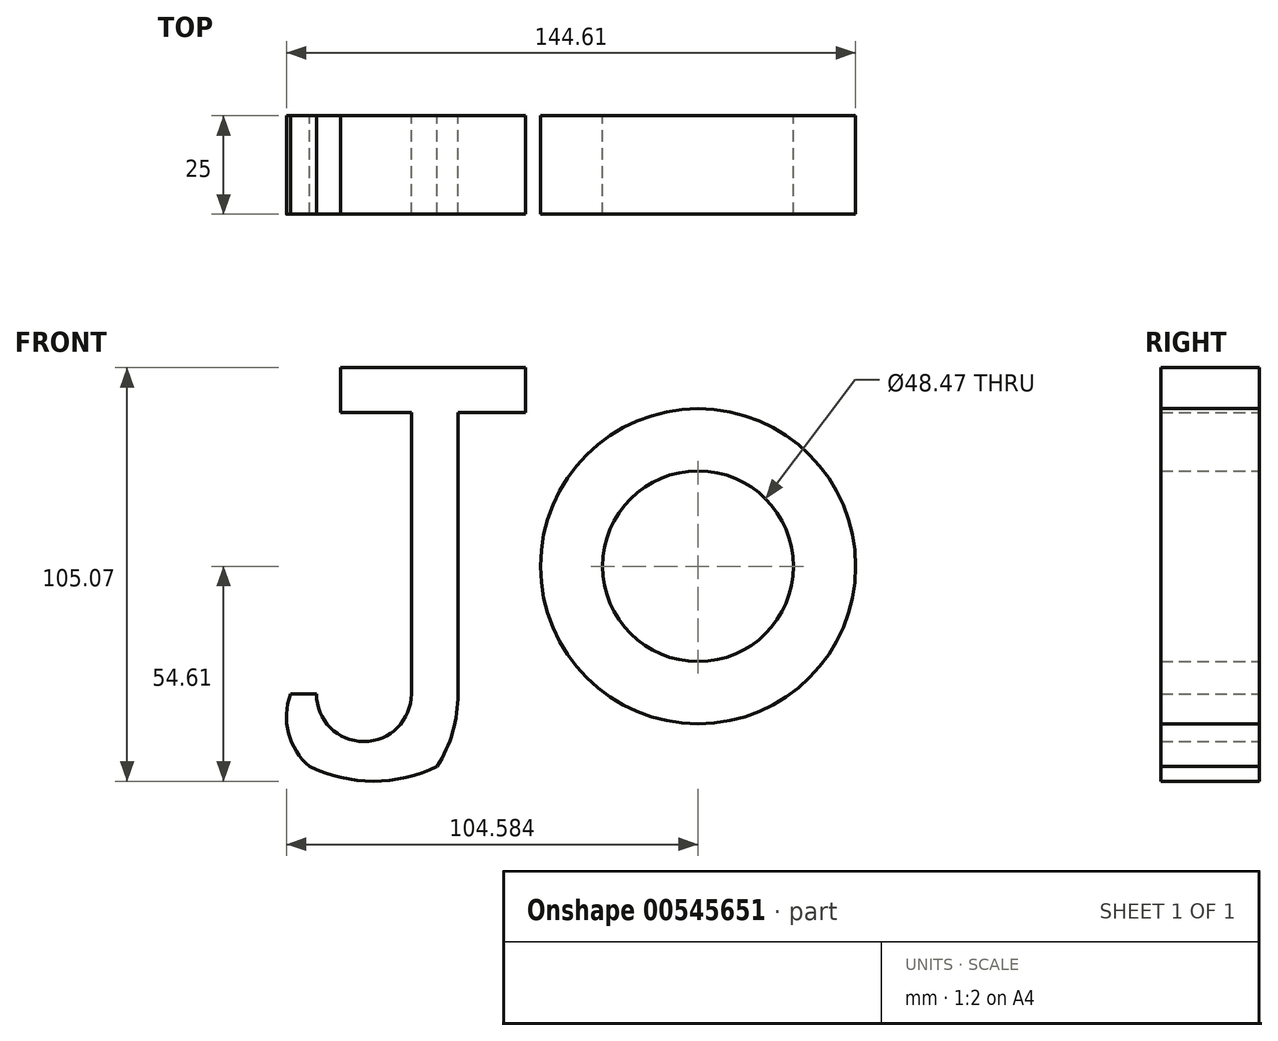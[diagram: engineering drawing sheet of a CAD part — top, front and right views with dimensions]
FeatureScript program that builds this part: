
annotation { "Feature Type Name" : "Feature", "Feature Type Description" : "" }
export const myFeature = defineFeature(function(context is Context, id is Id, definition is map)
    precondition{}
    {
        {
            var Q0;
            Q0=qCreatedBy(makeId("Front.planeOp"),FACE);
            var sketch = newSketch(context, id + "F0", { "sketchPlane" : qUnion([Q0])});
            skLineSegment(sketch, "E0.bottom", {"start": v(-63.19, 50.46) * mm, "end": v(-16.24, 50.46) * mm});
            skLineSegment(sketch, "E0.top", {"start": v(-63.19, 39.05) * mm, "end": v(-16.24, 39.05) * mm});
            skLineSegment(sketch, "E0.left", {"start": v(-63.19, 50.46) * mm, "end": v(-63.19, 39.05) * mm});
            skLineSegment(sketch, "E0.right", {"start": v(-16.24, 50.46) * mm, "end": v(-16.24, 39.05) * mm});
            skLineSegment(sketch, "E1.bottom", {"start": v(-45.2, 39.05) * mm, "end": v(-33.35, 39.05) * mm});
            skLineSegment(sketch, "E1.left", {"start": v(-45.2, 39.05) * mm, "end": v(-45.2, -32.47) * mm});
            skLineSegment(sketch, "E1.right", {"start": v(-33.35, 39.05) * mm, "end": v(-33.35, -32.47) * mm});
            skArc(sketch, "E2", {"start": v(-45.2, -32.47) * mm, "mid": v(-57.26, -44.54) * mm, "end": v(-69.33, -32.47) * mm});
            skArc(sketch, "E3", {"start": v(-38.61, -50.9) * mm, "mid": v(-34.7, -42.05) * mm, "end": v(-33.35, -32.47) * mm});
            skArc(sketch, "E4", {"start": v(-71.09, -50.9) * mm, "mid": v(-54.85, -54.61) * mm, "end": v(-38.61, -50.9) * mm});
            skArc(sketch, "E5", {"start": v(-75.91, -32.47) * mm, "mid": v(-76.4, -42.45) * mm, "end": v(-71.09, -50.9) * mm});
            skLineSegment(sketch, "E6.bottom", {"start": v(-75.91, -32.47) * mm, "end": v(-69.33, -32.47) * mm});
            skLineSegment(sketch, "E6.top", {"start": v(-75.91, -32.47) * mm, "end": v(-69.33, -32.47) * mm});
            skLineSegment(sketch, "E6.left", {"start": v(-75.91, -32.47) * mm, "end": v(-75.91, -32.47) * mm});
            skLineSegment(sketch, "E6.right", {"start": v(-69.33, -32.47) * mm, "end": v(-69.33, -32.47) * mm});
            skCircle(sketch, "E7", {"center": v(27.64, 0) * mm, "radius": 40.02 * mm});
            skCircle(sketch, "E8", {"center": v(27.64, 0) * mm, "radius": 24.23 * mm});
            skSolve(sketch);
        }
        {
            var Q0;
            Q0 = qSketchRegion(id + "F0", true);
            extrude(context, id + "F1", {"entities" : qUnion([Q0]), "depth" : 25 * mm, "offsetDistance" : 25 * mm});
        }
    });
